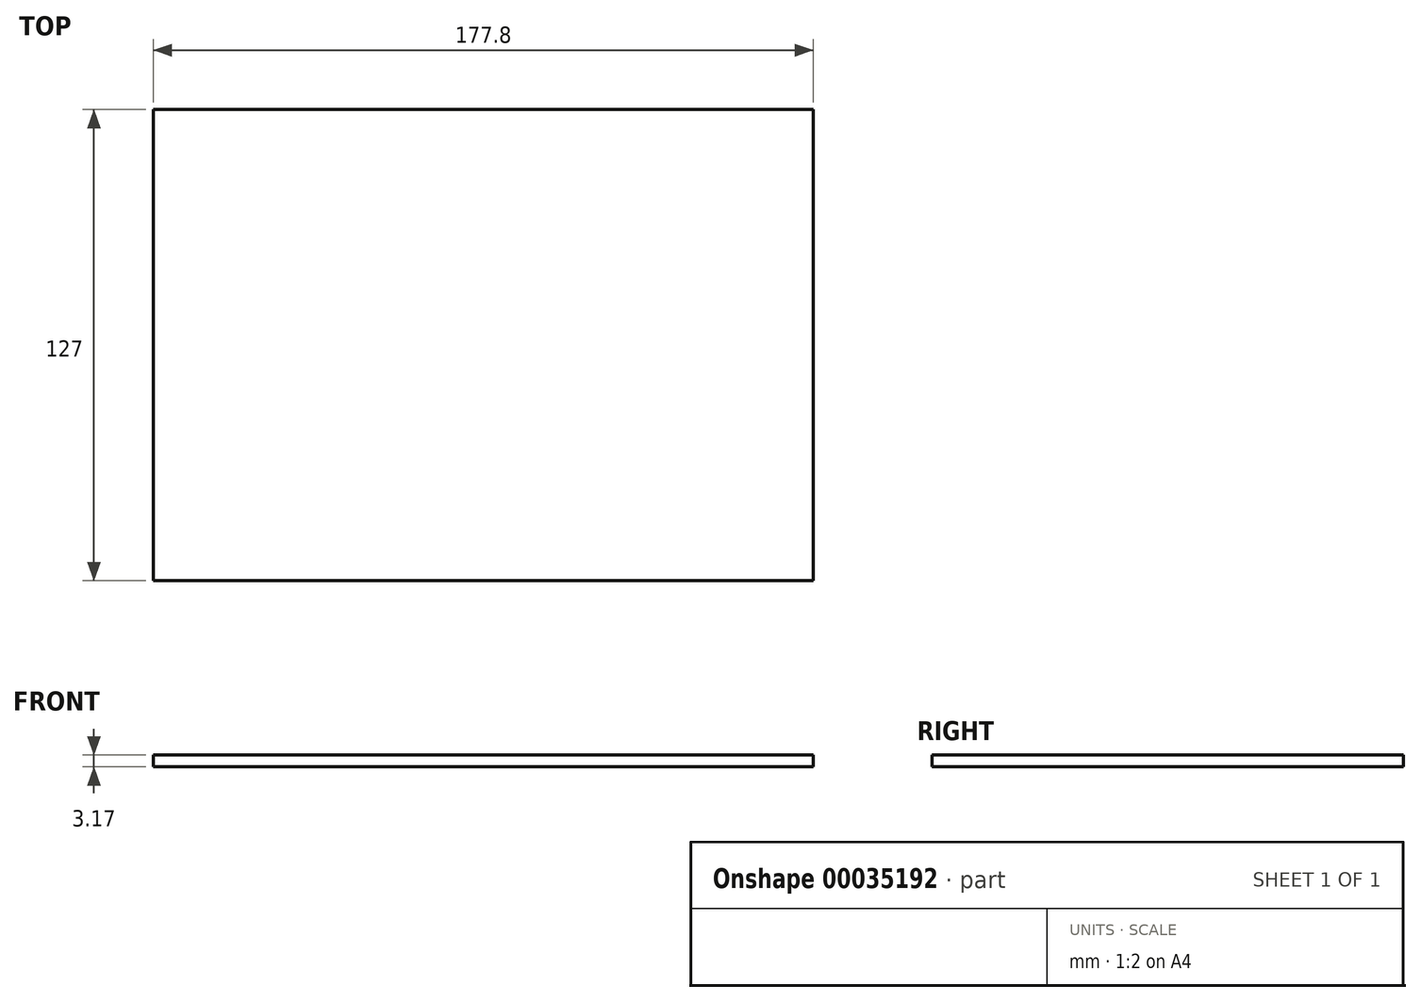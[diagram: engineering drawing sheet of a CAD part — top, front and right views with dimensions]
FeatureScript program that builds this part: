
annotation { "Feature Type Name" : "Feature", "Feature Type Description" : "" }
export const myFeature = defineFeature(function(context is Context, id is Id, definition is map)
    precondition{}
    {
        {
            var Q0;
            Q0=qCreatedBy(makeId("Top.planeOp"),FACE);
            var sketch = newSketch(context, id + "F0", { "sketchPlane" : qUnion([Q0])});
            skLineSegment(sketch, "E0.rect.bottom", {"start": v(88.9, -63.5) * mm, "end": v(-88.9, -63.5) * mm});
            skLineSegment(sketch, "E0.rect.top", {"start": v(88.9, 63.5) * mm, "end": v(-88.9, 63.5) * mm});
            skLineSegment(sketch, "E0.rect.left", {"start": v(88.9, -63.5) * mm, "end": v(88.9, 63.5) * mm});
            skLineSegment(sketch, "E0.rect.right", {"start": v(-88.9, -63.5) * mm, "end": v(-88.9, 63.5) * mm});
            skPoint(sketch, "E0.rect.middle", {"position": v(0, 0) * mm});
            skSolve(sketch);
        }
        {
            var Q0;
            Q0=makeQuery(id+"F0.imprint","IMPRINT",FACE,{"disambiguationData":[TD([[makeQuery(id+"F0.imprint","IMPRINT",EDGE,{"derivedFrom":sQuery(id+"F0.wireOp",EDGE,"E0.rect.bottom")}),-1.0]])]});
            extrude(context, id + "F1", {"entities" : qUnion([Q0]), "depth" : 3.17 * mm});
        }
    });
